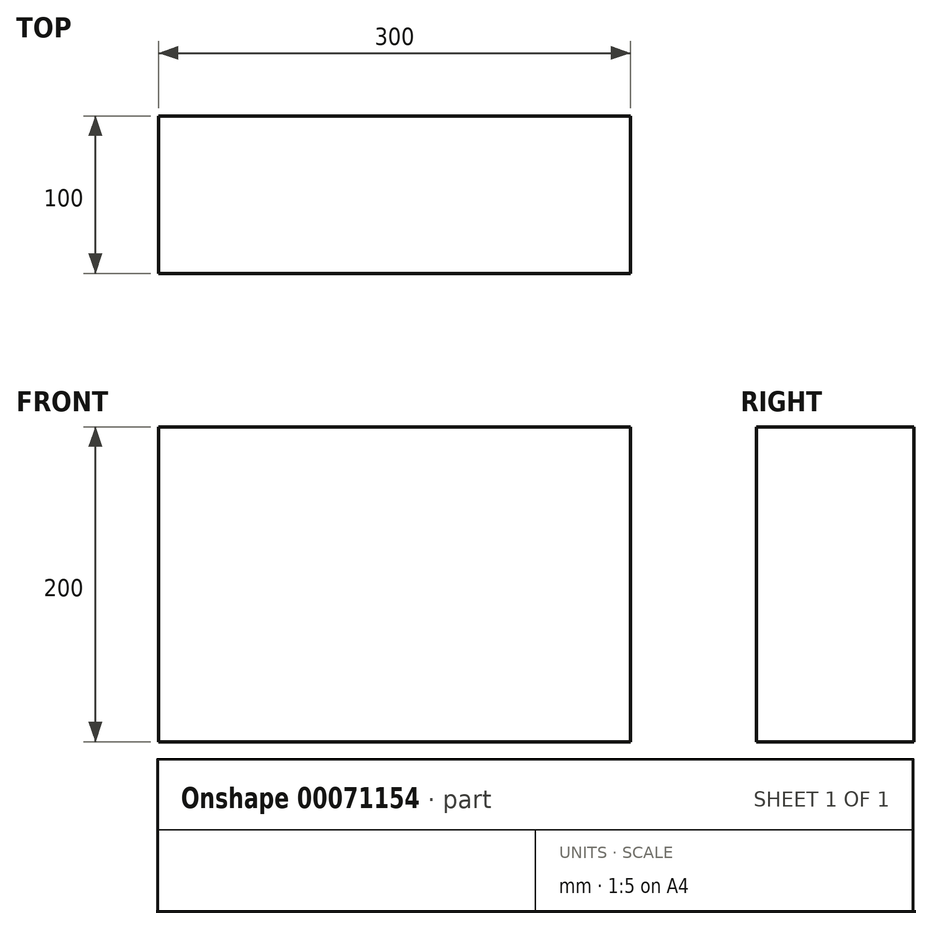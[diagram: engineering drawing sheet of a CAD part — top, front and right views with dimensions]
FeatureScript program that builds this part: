
annotation { "Feature Type Name" : "Feature", "Feature Type Description" : "" }
export const myFeature = defineFeature(function(context is Context, id is Id, definition is map)
    precondition{}
    {
        {
            var Q0;
            Q0=qCreatedBy(makeId("Front.planeOp"),FACE);
            var sketch = newSketch(context, id + "F0", { "sketchPlane" : qUnion([Q0])});
            skLineSegment(sketch, "E0.rect.bottom", {"start": v(-150, 100) * mm, "end": v(150, 100) * mm});
            skLineSegment(sketch, "E0.rect.top", {"start": v(-150, -100) * mm, "end": v(150, -100) * mm});
            skLineSegment(sketch, "E0.rect.left", {"start": v(-150, 100) * mm, "end": v(-150, -100) * mm});
            skLineSegment(sketch, "E0.rect.right", {"start": v(150, 100) * mm, "end": v(150, -100) * mm});
            skPoint(sketch, "E0.rect.middle", {"position": v(0, 0) * mm});
            skSolve(sketch);
        }
        {
            var Q0;
            Q0=makeQuery(id+"F0.imprint","IMPRINT",FACE,{"disambiguationData":[TD([[makeQuery(id+"F0.imprint","IMPRINT",EDGE,{"derivedFrom":sQuery(id+"F0.wireOp",EDGE,"E0.rect.bottom")}),-1.0]])]});
            extrude(context, id + "F1", {"entities" : qUnion([Q0]), "depth" : 100 * mm});
        }
        {
            var Q0;
            Q0=qCreatedBy(makeId("Front.planeOp"),FACE);
            var sketch = newSketch(context, id + "F2", { "sketchPlane" : qUnion([Q0])});
            skLineSegment(sketch, "E1.bottom", {"start": v(-150, 100) * mm, "end": v(-50, 100) * mm});
            skLineSegment(sketch, "E1.top", {"start": v(-150, 0) * mm, "end": v(-50, 0) * mm});
            skLineSegment(sketch, "E1.left", {"start": v(-150, 100) * mm, "end": v(-150, 0) * mm});
            skLineSegment(sketch, "E1.right", {"start": v(-50, 100) * mm, "end": v(-50, 0) * mm});
            skSolve(sketch);
        }
        {
            var Q0;
            Q0=qCreatedBy(makeId("Front.planeOp"),FACE);
            var sketch = newSketch(context, id + "F3", { "sketchPlane" : qUnion([Q0])});
            skLineSegment(sketch, "E2.bottom", {"start": v(50, 100) * mm, "end": v(-50, 100) * mm});
            skLineSegment(sketch, "E2.top", {"start": v(50, 0) * mm, "end": v(-50, 0) * mm});
            skLineSegment(sketch, "E2.left", {"start": v(50, 100) * mm, "end": v(50, 0) * mm});
            skLineSegment(sketch, "E2.right", {"start": v(-50, 100) * mm, "end": v(-50, 0) * mm});
            skSolve(sketch);
        }
        {
            var Q0;
            Q0=qCreatedBy(makeId("Front.planeOp"),FACE);
            var sketch = newSketch(context, id + "F4", { "sketchPlane" : qUnion([Q0])});
            skLineSegment(sketch, "E3.bottom", {"start": v(-50, 0) * mm, "end": v(50, 0) * mm});
            skLineSegment(sketch, "E3.top", {"start": v(-50, -100) * mm, "end": v(50, -100) * mm});
            skLineSegment(sketch, "E3.left", {"start": v(-50, 0) * mm, "end": v(-50, -100) * mm});
            skLineSegment(sketch, "E3.right", {"start": v(50, 0) * mm, "end": v(50, -100) * mm});
            skSolve(sketch);
        }
        {
            var Q0;
            Q0=makeQuery(id+"F0.imprint","IMPRINT",FACE,{"disambiguationData":[TD([[makeQuery(id+"F0.imprint","IMPRINT",EDGE,{"derivedFrom":sQuery(id+"F0.wireOp",EDGE,"E0.rect.bottom")}),-1.0]])]});
            cPlane(context, id + "F5", {"entities" : qUnion([Q0]), "cplaneType" : CPlaneType.OFFSET, "offset" : 100 * mm, "width" : 150 * mm, "height" : 150 * mm});
        }
    });
